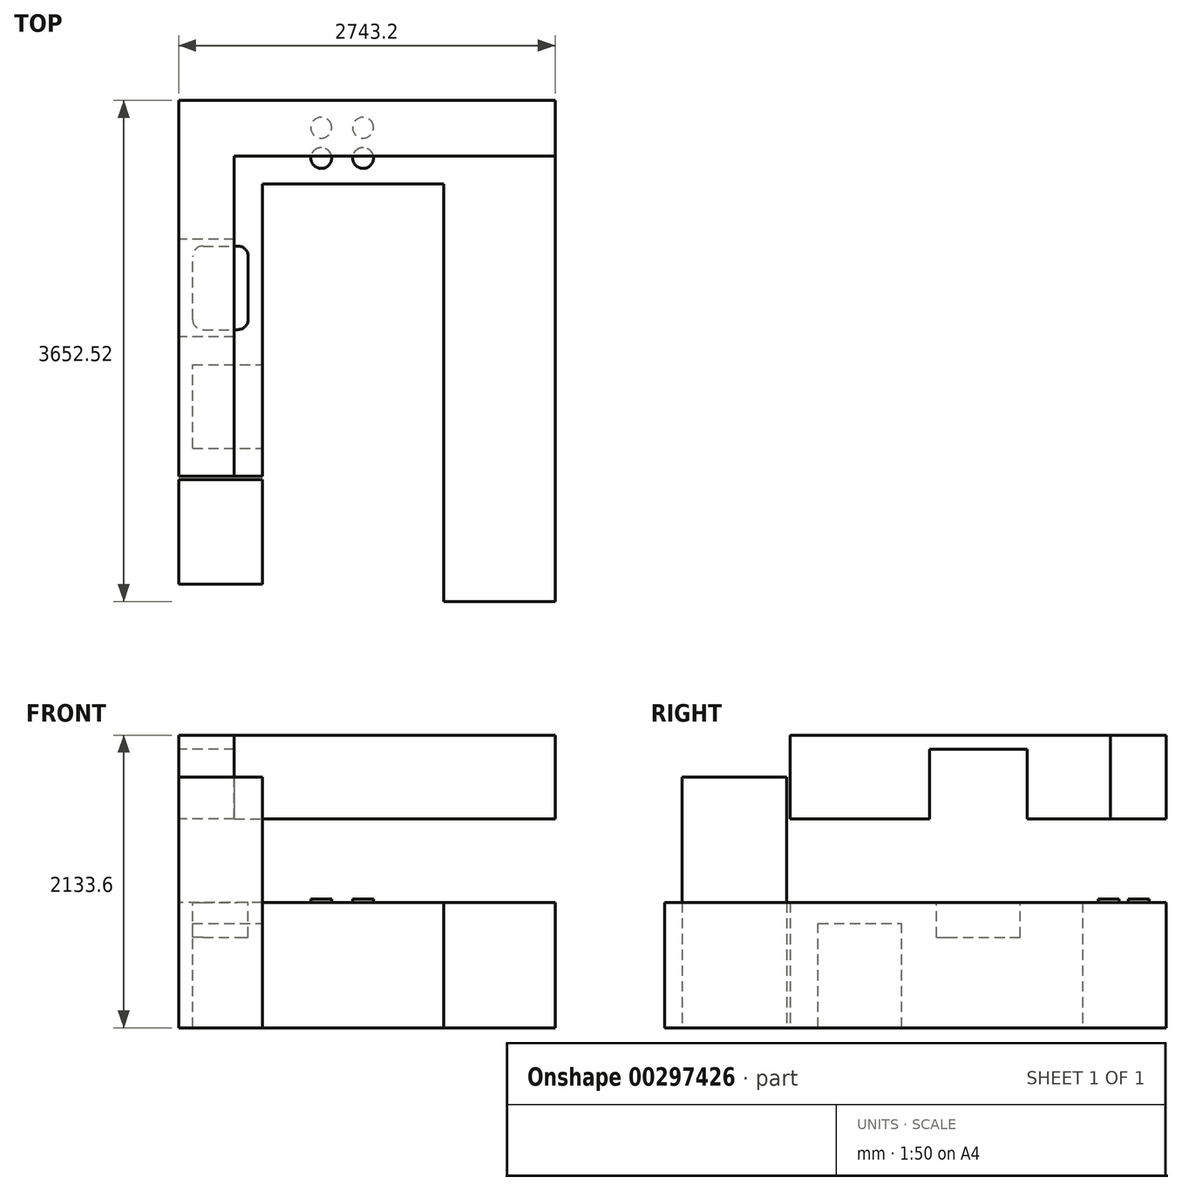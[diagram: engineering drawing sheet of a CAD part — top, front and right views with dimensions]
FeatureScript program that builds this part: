
annotation { "Feature Type Name" : "Feature", "Feature Type Description" : "" }
export const myFeature = defineFeature(function(context is Context, id is Id, definition is map)
    precondition{}
    {
        {
            var Q0;
            Q0=qCreatedBy(makeId("Top.planeOp"),FACE);
            var sketch = newSketch(context, id + "F0", { "sketchPlane" : qUnion([Q0])});
            skLineSegment(sketch, "E0.bottom", {"start": v(1371.6, -1826.26) * mm, "end": v(558.8, -1826.26) * mm});
            skLineSegment(sketch, "E0.top", {"start": v(1371.6, 1826.26) * mm, "end": v(-1371.6, 1826.26) * mm});
            skLineSegment(sketch, "E0.left", {"start": v(1371.6, -1826.26) * mm, "end": v(1371.6, 1826.26) * mm});
            skLineSegment(sketch, "E0.right", {"start": v(-1371.6, -911.86) * mm, "end": v(-1371.6, 1826.26) * mm});
            skPoint(sketch, "E0.middle", {"position": v(0, 0) * mm});
            skLineSegment(sketch, "E1.0", {"start": v(-762, -911.86) * mm, "end": v(-762, 1216.66) * mm});
            skLineSegment(sketch, "E2.0", {"start": v(558.8, 1216.66) * mm, "end": v(-762, 1216.66) * mm});
            skLineSegment(sketch, "E3.0", {"start": v(558.8, -1826.26) * mm, "end": v(558.8, 1216.66) * mm});
            skLineSegment(sketch, "E4.0", {"start": v(-762, -911.86) * mm, "end": v(-1371.6, -911.86) * mm});
            skPoint(sketch, "E5.orphan", {"position": v(-1371.6, -1826.26) * mm});
            skSolve(sketch);
        }
        {
            var Q0;
            Q0=qSketchRegion(id+"F0",true);
            extrude(context, id + "F1", {"entities" : qUnion([Q0]), "depth" : 914.4 * mm});
        }
        {
            var Q0;
            Q0=qCreatedBy(makeId("Top.planeOp"),FACE);
            var sketch = newSketch(context, id + "F2", { "sketchPlane" : qUnion([Q0])});
            skLineSegment(sketch, "E6.top", {"start": v(-1371.6, -1699.26) * mm, "end": v(-762, -1699.26) * mm});
            skLineSegment(sketch, "E6.left", {"start": v(-1371.6, -937.26) * mm, "end": v(-1371.6, -1699.26) * mm});
            skLineSegment(sketch, "E6.right", {"start": v(-762, -937.26) * mm, "end": v(-762, -1699.26) * mm});
            skLineSegment(sketch, "E7", {"start": v(-1371.6, -937.26) * mm, "end": v(-762, -937.26) * mm});
            skSolve(sketch);
        }
        {
            var Q0;
            Q0=qSketchRegion(id+"F2",true);
            extrude(context, id + "F3", {"entities" : qUnion([Q0]), "operationType" : NewBodyOperationType.ADD, "depth" : 1828.8 * mm});
        }
        {
            var Q0;
            Q0=makeQuery(id+"F1.opExtrude","SWEPT_FACE",FACE,{"disambiguationData":[OSD([sQuery(id+"F0.wireOp",EDGE,"E1.0")])]});
            var sketch = newSketch(context, id + "F4", { "sketchPlane" : qUnion([Q0])});
            skLineSegment(sketch, "E8.bottom", {"start": v(-708.66, 0) * mm, "end": v(-99.06, 0) * mm});
            skLineSegment(sketch, "E8.top", {"start": v(-708.66, 762) * mm, "end": v(-99.06, 762) * mm});
            skLineSegment(sketch, "E8.left", {"start": v(-708.66, 0) * mm, "end": v(-708.66, 762) * mm});
            skLineSegment(sketch, "E8.right", {"start": v(-99.06, 0) * mm, "end": v(-99.06, 762) * mm});
            skSolve(sketch);
        }
        {
            var Q0;
            Q0=qSketchRegion(id+"F4",true);
            extrude(context, id + "F5", {"entities" : qUnion([Q0]), "operationType" : NewBodyOperationType.REMOVE, "oppositeDirection" : true, "depth" : 508 * mm});
        }
        {
            var Q0;
            Q0=makeQuery(id+"F1.opExtrude","CAP_FACE",FACE,{"disambiguationData":[OSD([sQuery(id+"F0.wireOp",EDGE,"E0.bottom"),sQuery(id+"F0.wireOp",EDGE,"E0.top"),sQuery(id+"F0.wireOp",EDGE,"E0.left"),sQuery(id+"F0.wireOp",EDGE,"E0.right"),sQuery(id+"F0.wireOp",EDGE,"E1.0"),sQuery(id+"F0.wireOp",EDGE,"E2.0"),sQuery(id+"F0.wireOp",EDGE,"E3.0"),sQuery(id+"F0.wireOp",EDGE,"E4.0")])],"isStart":false});
            var sketch = newSketch(context, id + "F6", { "sketchPlane" : qUnion([Q0])});
            skLineSegment(sketch, "E9.bottom", {"start": v(-1193.8, 154.94) * mm, "end": v(-939.8, 154.94) * mm});
            skLineSegment(sketch, "E9.top", {"start": v(-1193.8, 764.54) * mm, "end": v(-939.8, 764.54) * mm});
            skLineSegment(sketch, "E9.left", {"start": v(-1270, 231.14) * mm, "end": v(-1270, 688.34) * mm});
            skLineSegment(sketch, "E9.right", {"start": v(-863.6, 231.14) * mm, "end": v(-863.6, 688.34) * mm});
            skPoint(sketch, "E10.visualSharp", {"position": v(-1270, 154.94) * mm});
            skArc(sketch, "E10.filletArc", {"start": v(-1270, 231.14) * mm, "mid": v(-1247.68, 177.26) * mm, "end": v(-1193.8, 154.94) * mm});
            skPoint(sketch, "E11.visualSharp", {"position": v(-863.6, 154.94) * mm});
            skArc(sketch, "E11.filletArc", {"start": v(-939.8, 154.94) * mm, "mid": v(-885.92, 177.26) * mm, "end": v(-863.6, 231.14) * mm});
            skPoint(sketch, "E12.visualSharp", {"position": v(-863.6, 764.54) * mm});
            skArc(sketch, "E12.filletArc", {"start": v(-863.6, 688.34) * mm, "mid": v(-885.92, 742.22) * mm, "end": v(-939.8, 764.54) * mm});
            skPoint(sketch, "E13.visualSharp", {"position": v(-1270, 764.54) * mm});
            skArc(sketch, "E13.filletArc", {"start": v(-1193.8, 764.54) * mm, "mid": v(-1247.68, 742.22) * mm, "end": v(-1270, 688.34) * mm});
            skSolve(sketch);
        }
        {
            var Q0;
            Q0=qSketchRegion(id+"F6",true);
            extrude(context, id + "F7", {"entities" : qUnion([Q0]), "operationType" : NewBodyOperationType.REMOVE, "oppositeDirection" : true, "depth" : 254 * mm});
        }
        {
            var Q0;
            Q0=makeQuery(id+"F1.opExtrude","CAP_FACE",FACE,{"disambiguationData":[OSD([sQuery(id+"F0.wireOp",EDGE,"E0.bottom"),sQuery(id+"F0.wireOp",EDGE,"E0.top"),sQuery(id+"F0.wireOp",EDGE,"E0.left"),sQuery(id+"F0.wireOp",EDGE,"E0.right"),sQuery(id+"F0.wireOp",EDGE,"E1.0"),sQuery(id+"F0.wireOp",EDGE,"E2.0"),sQuery(id+"F0.wireOp",EDGE,"E3.0"),sQuery(id+"F0.wireOp",EDGE,"E4.0")])],"isStart":false});
            var sketch = newSketch(context, id + "F8", { "sketchPlane" : qUnion([Q0])});
            skCircle(sketch, "E14", {"center": v(-331.95, 1406.1) * mm, "radius": 76.2 * mm});
            skCircle(sketch, "E15", {"center": v(-331.95, 1627.46) * mm, "radius": 76.2 * mm});
            skCircle(sketch, "E16", {"center": v(-27.15, 1406.1) * mm, "radius": 76.2 * mm});
            skCircle(sketch, "E17", {"center": v(-27.15, 1627.46) * mm, "radius": 76.2 * mm});
            skSolve(sketch);
        }
        {
            var Q0;
            Q0=qSketchRegion(id+"F8",true);
            extrude(context, id + "F9", {"entities" : qUnion([Q0]), "operationType" : NewBodyOperationType.ADD, "depth" : 25.4 * mm});
        }
        {
            var Q0;
            Q0=makeQuery(id+"F1.opExtrude","SWEPT_FACE",FACE,{"disambiguationData":[OSD([sQuery(id+"F0.wireOp",EDGE,"E0.right")])]});
            var sketch = newSketch(context, id + "F10", { "sketchPlane" : qUnion([Q0])});
            skLineSegment(sketch, "E18.bottom", {"start": v(-1826.26, 2133.6) * mm, "end": v(911.86, 2133.6) * mm});
            skLineSegment(sketch, "E18.top", {"start": v(-104.14, 1524) * mm, "end": v(911.86, 1524) * mm});
            skLineSegment(sketch, "E18.left", {"start": v(911.86, 2133.6) * mm, "end": v(911.86, 1524) * mm});
            skLineSegment(sketch, "E18.right", {"start": v(-1826.26, 2133.6) * mm, "end": v(-1826.26, 1524) * mm});
            skLineSegment(sketch, "E19.top", {"start": v(-815.34, 2032) * mm, "end": v(-104.14, 2032) * mm});
            skLineSegment(sketch, "E19.left", {"start": v(-815.34, 1524) * mm, "end": v(-815.34, 2032) * mm});
            skLineSegment(sketch, "E19.right", {"start": v(-104.14, 1524) * mm, "end": v(-104.14, 2032) * mm});
            skLineSegment(sketch, "E20.trimOffspring", {"start": v(-1826.26, 1524) * mm, "end": v(-815.34, 1524) * mm});
            skSolve(sketch);
        }
        {
            var Q0;
            Q0=qSketchRegion(id+"F10",true);
            extrude(context, id + "F11", {"entities" : qUnion([Q0]), "oppositeDirection" : true, "depth" : 406.4 * mm});
        }
        {
            var Q0;
            Q0=makeQuery(id+"F1.opExtrude","SWEPT_FACE",FACE,{"disambiguationData":[OSD([sQuery(id+"F0.wireOp",EDGE,"E0.top")])]});
            var sketch = newSketch(context, id + "F12", { "sketchPlane" : qUnion([Q0])});
            skLineSegment(sketch, "E21.bottom", {"start": v(965.2, 2133.6) * mm, "end": v(-1371.6, 2133.6) * mm});
            skLineSegment(sketch, "E21.top", {"start": v(965.2, 1524) * mm, "end": v(-1371.6, 1524) * mm});
            skLineSegment(sketch, "E21.left", {"start": v(965.2, 2133.6) * mm, "end": v(965.2, 1524) * mm});
            skLineSegment(sketch, "E21.right", {"start": v(-1371.6, 2133.6) * mm, "end": v(-1371.6, 1524) * mm});
            skSolve(sketch);
        }
        {
            var Q0;
            Q0=qSketchRegion(id+"F12",true);
            extrude(context, id + "F13", {"entities" : qUnion([Q0]), "operationType" : NewBodyOperationType.ADD, "oppositeDirection" : true, "depth" : 406.4 * mm});
        }
    });
